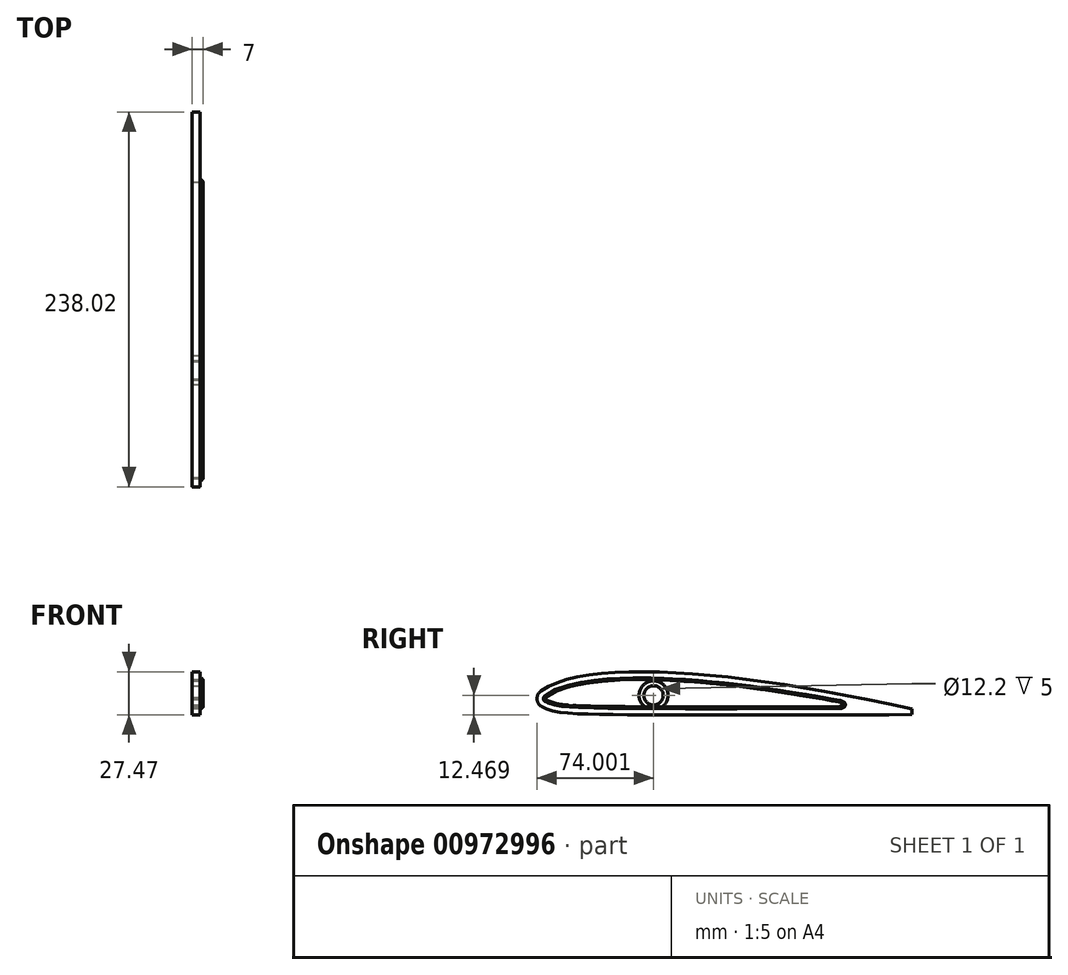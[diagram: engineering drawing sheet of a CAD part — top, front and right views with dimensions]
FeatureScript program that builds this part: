
annotation { "Feature Type Name" : "Feature", "Feature Type Description" : "" }
export const myFeature = defineFeature(function(context is Context, id is Id, definition is map)
    precondition{}
    {
        {
            var Q0;
            Q0=qCreatedBy(makeId("Right.planeOp"),FACE);
            var sketch = newSketch(context, id + "F0", { "sketchPlane" : qUnion([Q0])});
            skLineSegment(sketch, "E0", {"start": v(0, 0) * mm, "end": v(238.13, 0) * mm, "construction": true});
            skLineSegment(sketch, "E1", {"start": v(0, 0) * mm, "end": v(0, 0) * mm, "construction": true});
            skLineSegment(sketch, "E2", {"start": v(238, 3.78) * mm, "end": v(238, 0) * mm});
            skArc(sketch, "E3", {"start": v(2.42, 14.91) * mm, "mid": v(0, 9.87) * mm, "end": v(2.87, 5.07) * mm});
            skFitSpline(sketch, "E4", {"points": [v(238, 3.78) * mm, v(106.78, 25.25) * mm, v(33.8, 25.33) * mm, v(2.42, 14.91) * mm], "startDerivative": vector(-337.3, 72.63) * mm, "endDerivative": vector(-98.74, -71.57) * mm});
            skFitSpline(sketch, "E5", {"points": [v(238, 0) * mm, v(38.76, 0.2) * mm, v(2.87, 5.07) * mm], "startDerivative": vector(-331.95, -0.25) * mm, "endDerivative": vector(-67.54, 40.03) * mm});
            skSolve(sketch);
        }
        {
            var Q0;
            Q0=makeQuery(id+"F0.imprint","IMPRINT",FACE,{"disambiguationData":[TD([[makeQuery(id+"F0.imprint","IMPRINT",EDGE,{"derivedFrom":sQuery(id+"F0.wireOp",EDGE,"E2")}),-1.0]])]});
            extrude(context, id + "F1", {"entities" : qUnion([Q0]), "depth" : 5 * mm, "offsetDistance" : 25 * mm});
        }
        {
            var Q0;
            Q0=qCreatedBy(makeId("Right.planeOp"),FACE);
            var sketch = newSketch(context, id + "F2", { "sketchPlane" : qUnion([Q0])});
            skCircle(sketch, "E6", {"center": v(74, 12.26) * mm, "radius": 7.55 * mm});
            skLineSegment(sketch, "E7", {"start": v(27.72, 27.26) * mm, "end": v(191.9, 27.26) * mm, "construction": true});
            skLineSegment(sketch, "E8", {"start": v(56.37, 12.26) * mm, "end": v(199.63, 12.26) * mm, "construction": true});
            skLineSegment(sketch, "E9", {"start": v(54.7, 18.66) * mm, "end": v(212.58, 18.66) * mm, "construction": true});
            skSolve(sketch);
        }
        {
            var Q0;
            Q0=qSketchRegion(id+"F2",true);
            extrude(context, id + "F3", {"entities" : qUnion([Q0]), "operationType" : NewBodyOperationType.REMOVE, "endBound" : BoundingType.THROUGH_ALL, "depth" : 25 * mm, "offsetDistance" : 25 * mm, "hasSecondDirection" : true, "secondDirectionBound" : BoundingType.THROUGH_ALL, "secondDirectionOppositeDirection" : true, "secondDirectionDepth" : 25 * mm});
        }
        {
            var Q0;
            Q0=makeQuery(id+"F1.opExtrude","CAP_FACE",FACE,{"disambiguationData":[OSD([sQuery(id+"F0.wireOp",EDGE,"E2"),sQuery(id+"F0.wireOp",EDGE,"E3"),sQuery(id+"F0.wireOp",EDGE,"E4"),sQuery(id+"F0.wireOp",EDGE,"E5")])],"isStart":false});
            var sketch = newSketch(context, id + "F4", { "sketchPlane" : qUnion([Q0])});
            skFitSpline(sketch, "E10.0", {"points": [v(237.16, -0.13) * mm, v(223.14, 2.89) * mm, v(202.94, 7) * mm, v(177.56, 11.64) * mm, v(159.27, 14.68) * mm, v(141.7, 17.28) * mm, v(124.83, 19.43) * mm, v(108.61, 21.13) * mm, v(93.02, 22.37) * mm, v(78.16, 23.13) * mm, v(64.12, 23.35) * mm, v(51.04, 23.01) * mm, v(39.03, 22.08) * mm, v(28.2, 20.52) * mm, v(18.73, 18.3) * mm, v(10.77, 15.4) * mm, v(6.58, 12.99) * mm, v(4.77, 11.67) * mm]});
            skFitSpline(sketch, "E10.1", {"points": [v(238, 4) * mm, v(224.17, 3.99) * mm, v(196.38, 3.94) * mm, v(155.67, 3.84) * mm, v(123.67, 3.79) * mm, v(99.89, 3.79) * mm, v(83.13, 3.82) * mm, v(67.63, 3.88) * mm, v(55.88, 3.98) * mm, v(47.28, 4.07) * mm, v(41.25, 4.16) * mm, v(35.66, 4.26) * mm, v(30.52, 4.39) * mm, v(25.84, 4.56) * mm, v(20.17, 4.88) * mm, v(14.16, 5.5) * mm, v(9.54, 6.52) * mm, v(6.65, 7.58) * mm, v(5.46, 8.19) * mm, v(4.91, 8.5) * mm]});
            skArc(sketch, "E10.2", {"start": v(4.77, 11.67) * mm, "mid": v(3.99, 10.05) * mm, "end": v(4.91, 8.5) * mm});
            skArc(sketch, "E11.0", {"start": v(83.28, 3.82) * mm, "mid": v(86.52, 11.46) * mm, "end": v(84.28, 19.45) * mm});
            skLineSegment(sketch, "E12.0", {"start": v(59.94, 23.2) * mm, "end": v(10.02, 6.48) * mm});
            skLineSegment(sketch, "E13.0", {"start": v(63.49, 19.12) * mm, "end": v(20.94, 4.87) * mm});
            skLineSegment(sketch, "E14.0", {"start": v(84.28, 19.45) * mm, "end": v(146.9, 3.83) * mm});
            skLineSegment(sketch, "E15.0", {"start": v(93.69, 22.26) * mm, "end": v(167.39, 3.87) * mm});
            skFitSpline(sketch, "E16.trimOffspring", {"points": [v(238, 4) * mm, v(224.17, 3.99) * mm, v(196.38, 3.94) * mm, v(155.67, 3.84) * mm, v(123.67, 3.79) * mm, v(99.89, 3.79) * mm, v(83.13, 3.82) * mm, v(67.63, 3.88) * mm, v(55.88, 3.98) * mm, v(47.28, 4.07) * mm, v(41.25, 4.16) * mm, v(35.66, 4.26) * mm, v(30.52, 4.39) * mm, v(25.84, 4.56) * mm, v(20.17, 4.88) * mm, v(14.16, 5.5) * mm, v(9.54, 6.52) * mm, v(6.65, 7.58) * mm, v(5.46, 8.19) * mm, v(4.91, 8.5) * mm]});
            skFitSpline(sketch, "E17.trimOffspring", {"points": [v(237.16, -0.13) * mm, v(223.14, 2.89) * mm, v(202.94, 7) * mm, v(177.56, 11.64) * mm, v(159.27, 14.68) * mm, v(141.7, 17.28) * mm, v(124.83, 19.43) * mm, v(108.61, 21.13) * mm, v(93.02, 22.37) * mm, v(78.16, 23.13) * mm, v(64.12, 23.35) * mm, v(51.04, 23.01) * mm, v(39.03, 22.08) * mm, v(28.2, 20.52) * mm, v(18.73, 18.3) * mm, v(10.77, 15.4) * mm, v(6.58, 12.99) * mm, v(4.77, 11.67) * mm]});
            skFitSpline(sketch, "E18.trimOffspring", {"points": [v(238, 4) * mm, v(224.17, 3.99) * mm, v(196.38, 3.94) * mm, v(155.67, 3.84) * mm, v(123.67, 3.79) * mm, v(99.89, 3.79) * mm, v(83.13, 3.82) * mm, v(67.63, 3.88) * mm, v(55.88, 3.98) * mm, v(47.28, 4.07) * mm, v(41.25, 4.16) * mm, v(35.66, 4.26) * mm, v(30.52, 4.39) * mm, v(25.84, 4.56) * mm, v(20.17, 4.88) * mm, v(14.16, 5.5) * mm, v(9.54, 6.52) * mm, v(6.65, 7.58) * mm, v(5.46, 8.19) * mm, v(4.91, 8.5) * mm]});
            skArc(sketch, "E19.trimOffspring", {"start": v(63.49, 19.12) * mm, "mid": v(61.48, 11.33) * mm, "end": v(64.62, 3.91) * mm});
            skFitSpline(sketch, "E20.trimOffspring", {"points": [v(238, 4) * mm, v(224.17, 3.99) * mm, v(196.38, 3.94) * mm, v(155.67, 3.84) * mm, v(123.67, 3.79) * mm, v(99.89, 3.79) * mm, v(83.13, 3.82) * mm, v(67.63, 3.88) * mm, v(55.88, 3.98) * mm, v(47.28, 4.07) * mm, v(41.25, 4.16) * mm, v(35.66, 4.26) * mm, v(30.52, 4.39) * mm, v(25.84, 4.56) * mm, v(20.17, 4.88) * mm, v(14.16, 5.5) * mm, v(9.54, 6.52) * mm, v(6.65, 7.58) * mm, v(5.46, 8.19) * mm, v(4.91, 8.5) * mm]});
            skSolve(sketch);
        }
        {
            var Q0;
            Q0=qSketchRegion(id+"F4",true);
            extrude(context, id + "F5", {"entities" : qUnion([Q0]), "operationType" : NewBodyOperationType.ADD, "depth" : 2 * mm, "offsetDistance" : 25 * mm, "hasDraft" : true, "draftAngle" : 5 * degree, "draftPullDirection" : true});
        }
        {
            var Q0;
            Q0=makeQuery(id+"F5.opExtrude","SWEPT_EDGE",EDGE,{"disambiguationData":[OSD([sQuery(id+"F4.wireOp",EDGE,"E10.0"),sQuery(id+"F4.wireOp",EDGE,"E15.0")])]});
            var Q1;
            Q1=makeQuery(id+"F5.opExtrude","SWEPT_EDGE",EDGE,{"disambiguationData":[OSD([sQuery(id+"F4.wireOp",EDGE,"E11.0"),sQuery(id+"F4.wireOp",EDGE,"E14.0")])]});
            var Q2;
            Q2=makeQuery(id+"F5.opExtrude","SWEPT_EDGE",EDGE,{"disambiguationData":[OSD([sQuery(id+"F4.wireOp",EDGE,"E11.0"),sQuery(id+"F4.wireOp",EDGE,"E18.trimOffspring")])]});
            var Q3;
            Q3=makeQuery(id+"F5.opExtrude","SWEPT_EDGE",EDGE,{"disambiguationData":[OSD([sQuery(id+"F4.wireOp",EDGE,"E12.0"),sQuery(id+"F4.wireOp",EDGE,"E17.trimOffspring")])]});
            var Q4;
            Q4=makeQuery(id+"F5.opExtrude","SWEPT_EDGE",EDGE,{"disambiguationData":[OSD([sQuery(id+"F4.wireOp",EDGE,"E13.0"),sQuery(id+"F4.wireOp",EDGE,"E19.trimOffspring")])]});
            var Q5;
            Q5=makeQuery(id+"F5.opExtrude","SWEPT_EDGE",EDGE,{"disambiguationData":[OSD([sQuery(id+"F4.wireOp",EDGE,"E13.0"),sQuery(id+"F4.wireOp",EDGE,"E16.trimOffspring")])]});
            var Q6;
            Q6=makeQuery(id+"F5.opExtrude","SWEPT_EDGE",EDGE,{"disambiguationData":[OSD([sQuery(id+"F4.wireOp",EDGE,"E12.0"),sQuery(id+"F4.wireOp",EDGE,"E20.trimOffspring")])]});
            var Q7;
            Q7=makeQuery(id+"F5.opExtrude","SWEPT_EDGE",EDGE,{"disambiguationData":[OSD([sQuery(id+"F4.wireOp",EDGE,"E16.trimOffspring"),sQuery(id+"F4.wireOp",EDGE,"E19.trimOffspring")])]});
            var Q8;
            Q8=makeQuery(id+"F5.opExtrude","SWEPT_EDGE",EDGE,{"disambiguationData":[OSD([sQuery(id+"F4.wireOp",EDGE,"E14.0"),sQuery(id+"F4.wireOp",EDGE,"E18.trimOffspring")])]});
            var Q9;
            Q9=makeQuery(id+"F5.opExtrude","SWEPT_EDGE",EDGE,{"disambiguationData":[OSD([sQuery(id+"F4.wireOp",EDGE,"E10.1"),sQuery(id+"F4.wireOp",EDGE,"E15.0")])]});
            var Q10;
            Q10=makeQuery(id+"F5.opExtrude","SWEPT_EDGE",EDGE,{"disambiguationData":[OSD([sQuery(id+"F4.wireOp",EDGE,"E10.0"),sQuery(id+"F4.wireOp",EDGE,"E10.1")])]});
            fillet(context, id + "F6", {"entities" : qUnion([Q0, Q1, Q2, Q3, Q4, Q5, Q6, Q7, Q8, Q9, Q10]), "radius" : 2.5 * mm, "tangentPropagation" : true, "allowEdgeOverflow" : false});
        }
        {
            var Q0;
            Q0=makeQuery(id+"F5.opExtrude","CAP_FACE",FACE,{"disambiguationData":[OSD([sQuery(id+"F4.wireOp",EDGE,"E10.0"),sQuery(id+"F4.wireOp",EDGE,"E10.1"),sQuery(id+"F4.wireOp",EDGE,"E15.0")])],"isStart":false});
            var Q1;
            Q1=makeQuery(id+"F5.opExtrude","CAP_FACE",FACE,{"disambiguationData":[OSD([sQuery(id+"F4.wireOp",EDGE,"E11.0"),sQuery(id+"F4.wireOp",EDGE,"E14.0"),sQuery(id+"F4.wireOp",EDGE,"E18.trimOffspring")])],"isStart":false});
            var Q2;
            Q2=makeQuery(id+"F5.opExtrude","CAP_FACE",FACE,{"disambiguationData":[OSD([sQuery(id+"F4.wireOp",EDGE,"E13.0"),sQuery(id+"F4.wireOp",EDGE,"E16.trimOffspring"),sQuery(id+"F4.wireOp",EDGE,"E19.trimOffspring")])],"isStart":false});
            var Q3;
            Q3=makeQuery(id+"F5.opExtrude","CAP_FACE",FACE,{"disambiguationData":[OSD([sQuery(id+"F4.wireOp",EDGE,"E10.2"),sQuery(id+"F4.wireOp",EDGE,"E12.0"),sQuery(id+"F4.wireOp",EDGE,"E17.trimOffspring"),sQuery(id+"F4.wireOp",EDGE,"E20.trimOffspring")])],"isStart":false});
            chamfer(context, id + "F7", {"entities" : qUnion([Q0, Q1, Q2, Q3]), "width" : 1 * mm, "tangentPropagation" : true});
        }
        {
            var Q0;
            Q0=makeQuery(id+"F5.opExtrude","CAP_FACE",FACE,{"disambiguationData":[OSD([sQuery(id+"F4.wireOp",EDGE,"E10.0"),sQuery(id+"F4.wireOp",EDGE,"E10.1"),sQuery(id+"F4.wireOp",EDGE,"E15.0")])],"isStart":false});
            var Q1;
            Q1=makeQuery(id+"F5.opExtrude","CAP_FACE",FACE,{"disambiguationData":[OSD([sQuery(id+"F4.wireOp",EDGE,"E11.0"),sQuery(id+"F4.wireOp",EDGE,"E14.0"),sQuery(id+"F4.wireOp",EDGE,"E18.trimOffspring")])],"isStart":false});
            var Q2;
            Q2=makeQuery(id+"F5.opExtrude","CAP_FACE",FACE,{"disambiguationData":[OSD([sQuery(id+"F4.wireOp",EDGE,"E13.0"),sQuery(id+"F4.wireOp",EDGE,"E16.trimOffspring"),sQuery(id+"F4.wireOp",EDGE,"E19.trimOffspring")])],"isStart":false});
            var Q3;
            Q3=makeQuery(id+"F5.opExtrude","CAP_FACE",FACE,{"disambiguationData":[OSD([sQuery(id+"F4.wireOp",EDGE,"E10.2"),sQuery(id+"F4.wireOp",EDGE,"E12.0"),sQuery(id+"F4.wireOp",EDGE,"E17.trimOffspring"),sQuery(id+"F4.wireOp",EDGE,"E20.trimOffspring")])],"isStart":false});
            extrude(context, id + "F8", {"entities" : qUnion([Q0, Q1, Q2, Q3]), "operationType" : NewBodyOperationType.REMOVE, "endBound" : BoundingType.THROUGH_ALL, "oppositeDirection" : true, "depth" : 25 * mm, "offsetDistance" : 25 * mm});
        }
        {
            var Q0;
            Q0=makeQuery(id+"F1.opExtrude","CAP_FACE",FACE,{"disambiguationData":[OSD([sQuery(id+"F0.wireOp",EDGE,"E2"),sQuery(id+"F0.wireOp",EDGE,"E3"),sQuery(id+"F0.wireOp",EDGE,"E4"),sQuery(id+"F0.wireOp",EDGE,"E5")])],"isStart":false});
            var sketch = newSketch(context, id + "F9", { "sketchPlane" : qUnion([Q0])});
            skCircle(sketch, "E21", {"center": v(74, 12.26) * mm, "radius": 9.2 * mm});
            skCircle(sketch, "E22", {"center": v(74, 12.26) * mm, "radius": 6.1 * mm});
            skSolve(sketch);
        }
        {
            var Q0;
            Q0 = qSketchRegion(id + "F9", true);
            var Q1;
            Q1=makeQuery(id+"F1.opExtrude","CAP_FACE",FACE,{"disambiguationData":[OSD([sQuery(id+"F0.wireOp",EDGE,"E2"),sQuery(id+"F0.wireOp",EDGE,"E3"),sQuery(id+"F0.wireOp",EDGE,"E4"),sQuery(id+"F0.wireOp",EDGE,"E5")])],"isStart":true});
            extrude(context, id + "F10", {"entities" : qUnion([Q0]), "operationType" : NewBodyOperationType.ADD, "endBound" : BoundingType.UP_TO_SURFACE, "oppositeDirection" : true, "depth" : 25 * mm, "endBoundEntityFace" : qUnion([Q1]), "offsetDistance" : 25 * mm});
        }
    });
